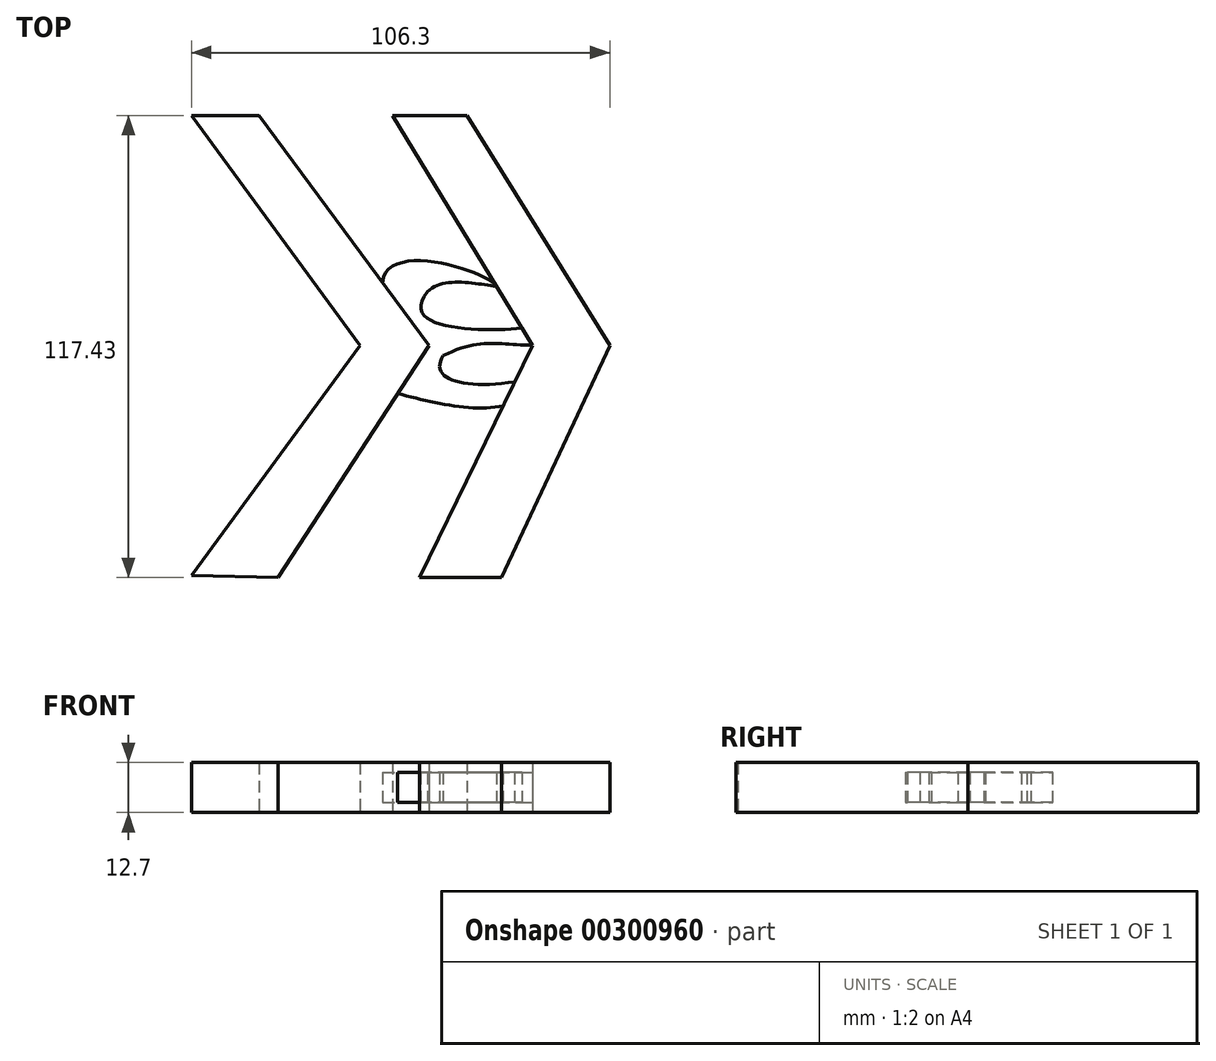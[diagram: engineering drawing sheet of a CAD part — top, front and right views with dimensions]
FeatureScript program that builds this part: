
annotation { "Feature Type Name" : "Feature", "Feature Type Description" : "" }
export const myFeature = defineFeature(function(context is Context, id is Id, definition is map)
    precondition{}
    {
        {
            var Q0;
            Q0=qCreatedBy(makeId("Top.planeOp"),FACE);
            var sketch = newSketch(context, id + "F0", { "sketchPlane" : qUnion([Q0])});
            skLineSegment(sketch, "E0", {"start": v(-63.96, 58.42) * mm, "end": v(-21.12, 0) * mm});
            skLineSegment(sketch, "E1", {"start": v(-21.12, 0) * mm, "end": v(-63.96, -58.5) * mm});
            skLineSegment(sketch, "E2", {"start": v(-63.96, 58.42) * mm, "end": v(-46.71, 58.42) * mm});
            skLineSegment(sketch, "E3", {"start": v(-46.71, 58.42) * mm, "end": v(-3.6, 0) * mm});
            skLineSegment(sketch, "E4", {"start": v(-3.6, 0) * mm, "end": v(-41.98, -59) * mm});
            skLineSegment(sketch, "E5", {"start": v(-41.98, -59) * mm, "end": v(-63.96, -58.5) * mm});
            skFitSpline(sketch, "E6", {"points": [v(-15.4, 15.99) * mm, v(13.56, 15) * mm], "startDerivative": vector(3.42, 32.92) * mm, "endDerivative": vector(6.9, -11.34) * mm});
            skFitSpline(sketch, "E7", {"points": [v(-11.58, -12.25) * mm, v(15.21, -15.38) * mm], "startDerivative": vector(26.03, -6.7) * mm, "endDerivative": vector(23.07, 5.14) * mm});
            skLineSegment(sketch, "E8", {"start": v(-12.85, 58.42) * mm, "end": v(22.68, 0) * mm});
            skPoint(sketch, "E8.startSnap0", {"position": v(-55.33, 58.42) * mm});
            skLineSegment(sketch, "E9", {"start": v(22.68, 0) * mm, "end": v(-5.98, -59) * mm});
            skLineSegment(sketch, "E10", {"start": v(-5.98, -59) * mm, "end": v(14.86, -59) * mm});
            skLineSegment(sketch, "E11", {"start": v(14.86, -59) * mm, "end": v(42.34, 0) * mm});
            skLineSegment(sketch, "E12", {"start": v(42.34, 0) * mm, "end": v(6.1, 58.42) * mm});
            skLineSegment(sketch, "E13", {"start": v(6.1, 58.42) * mm, "end": v(-12.85, 58.42) * mm});
            skFitSpline(sketch, "E14", {"points": [v(18.18, -9.27) * mm, v(0, -2.62) * mm], "startDerivative": vector(-39.56, -6.28) * mm, "endDerivative": vector(11.23, 17.97) * mm});
            skFitSpline(sketch, "E15", {"points": [v(0, -2.62) * mm, v(22.68, 0) * mm], "startDerivative": vector(27.71, 14.23) * mm, "endDerivative": vector(24.6, 0) * mm});
            skFitSpline(sketch, "E16", {"points": [v(20.03, 4.36) * mm, v(-4, 13.6) * mm], "startDerivative": vector(-29.38, -2.97) * mm, "endDerivative": vector(23.97, 29.96) * mm});
            skFitSpline(sketch, "E17", {"points": [v(-4, 13.6) * mm, v(13.56, 15) * mm], "startDerivative": vector(11.98, 11.96) * mm, "endDerivative": vector(15.96, -1.8) * mm});
            skSolve(sketch);
        }
        {
            var Q0;
            Q0=makeQuery(id+"F0.imprint","IMPRINT",FACE,{"disambiguationData":[TD([[makeQuery(id+"F0.imprint","IMPRINT",EDGE,{"derivedFrom":sQuery(id+"F0.wireOp",EDGE,"E0")}),1.0]])]});
            var Q1;
            {var subQ8=sQuery(id+"F0.wireOp",EDGE,"E10");Q1=makeQuery(id+"F0.imprint","IMPRINT",FACE,{"disambiguationData":[TD([[makeQuery(id+"F0.imprint","IMPRINT",EDGE,{"derivedFrom":subQ8}),1.0]])]});}
            extrude(context, id + "F1", {"entities" : qUnion([Q0, Q1]), "endBound" : BoundingType.SYMMETRIC, "depth" : 12.7 * mm});
        }
        {
            var Q0;
            {var subQ0=sQuery(id+"F0.wireOp",EDGE,"E6");Q0=makeQuery(id+"F0.imprint","IMPRINT",FACE,{"disambiguationData":[TD([[makeQuery(id+"F0.imprint","IMPRINT",EDGE,{"derivedFrom":subQ0}),-1.0]])]});}
            extrude(context, id + "F2", {"entities" : qUnion([Q0]), "endBound" : BoundingType.SYMMETRIC, "depth" : 7.62 * mm});
        }
    });
